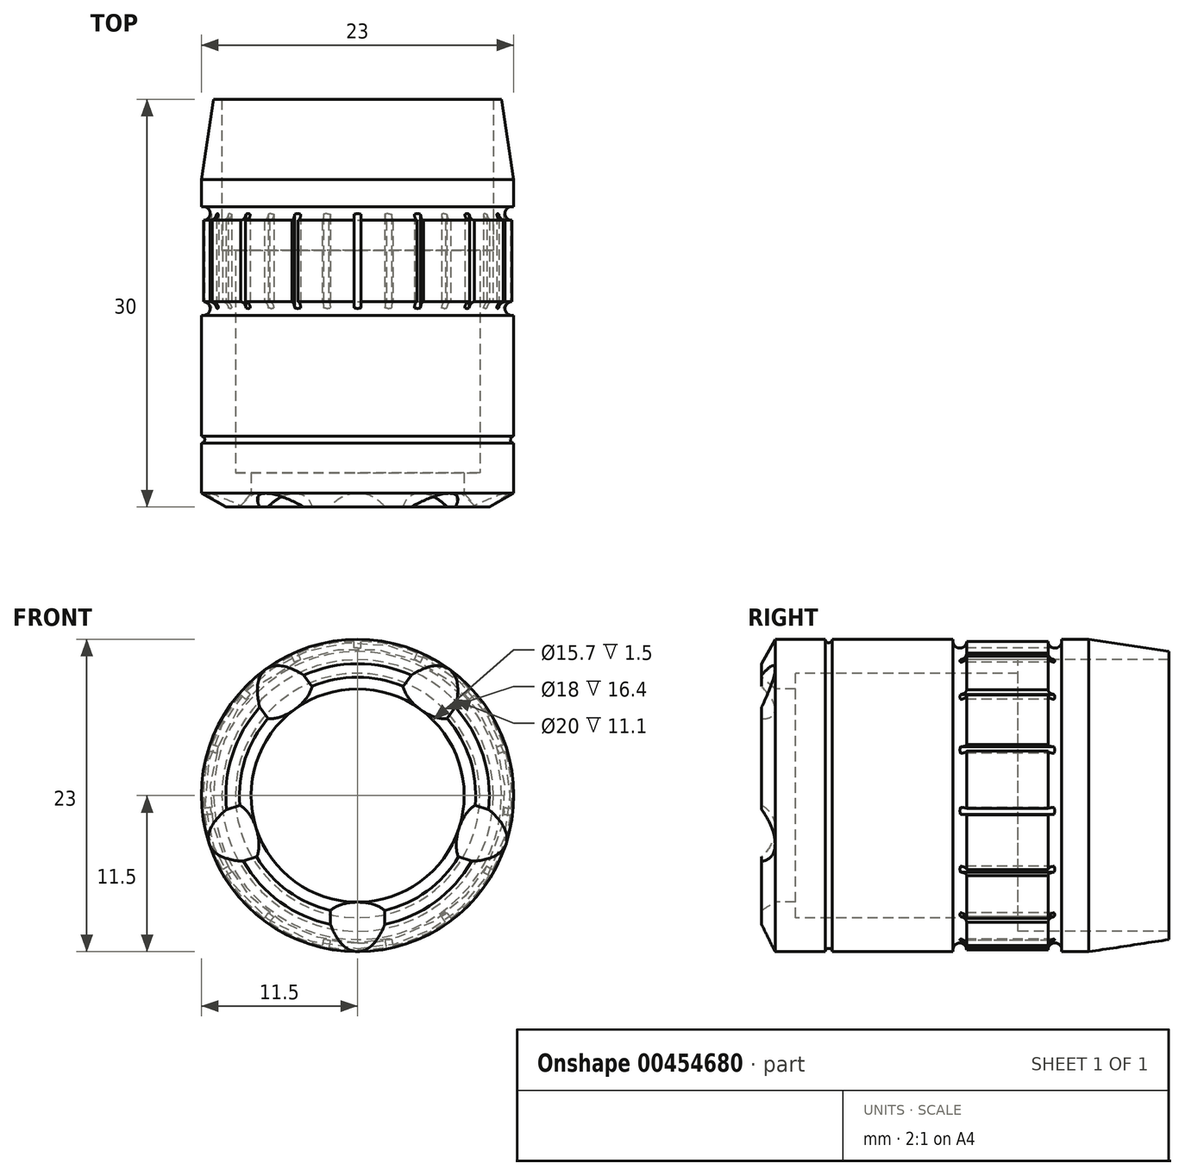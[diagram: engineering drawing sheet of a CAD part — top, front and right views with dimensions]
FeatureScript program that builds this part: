
annotation { "Feature Type Name" : "Feature", "Feature Type Description" : "" }
export const myFeature = defineFeature(function(context is Context, id is Id, definition is map)
    precondition{}
    {
        {
            var Q0;
            Q0=qCreatedBy(makeId("Right.planeOp"),FACE);
            var sketch = newSketch(context, id + "F0", { "sketchPlane" : qUnion([Q0])});
            skLineSegment(sketch, "E0", {"start": v(0, 7.85) * mm, "end": v(0, 11.5) * mm, "construction": true});
            skLineSegment(sketch, "E1", {"start": v(2.5, 7.85) * mm, "end": v(2.5, 9) * mm});
            skLineSegment(sketch, "E2", {"start": v(2.5, 9) * mm, "end": v(18.9, 9) * mm});
            skLineSegment(sketch, "E3", {"start": v(18.9, 9) * mm, "end": v(18.9, 10) * mm});
            skLineSegment(sketch, "E4", {"start": v(18.9, 10) * mm, "end": v(30, 10) * mm});
            skLineSegment(sketch, "E5", {"start": v(30, 10) * mm, "end": v(30, 10.6) * mm});
            skLineSegment(sketch, "E6", {"start": v(30, 10.6) * mm, "end": v(24.1, 11.5) * mm});
            skArc(sketch, "E7", {"start": v(4.7, 11.5) * mm, "mid": v(4.95, 11.25) * mm, "end": v(5.2, 11.5) * mm});
            skLineSegment(sketch, "E8", {"start": v(5.2, 11.5) * mm, "end": v(14.1, 11.5) * mm});
            skLineSegment(sketch, "E9", {"start": v(15.1, 11.35) * mm, "end": v(21.1, 11.35) * mm});
            skArc(sketch, "E10", {"start": v(14.1, 11.35) * mm, "mid": v(14.6, 10.85) * mm, "end": v(15.1, 11.35) * mm});
            skLineSegment(sketch, "E11", {"start": v(14.1, 11.35) * mm, "end": v(14.1, 11.5) * mm});
            skArc(sketch, "E12", {"start": v(21.1, 11.35) * mm, "mid": v(21.6, 10.85) * mm, "end": v(22.1, 11.35) * mm});
            skLineSegment(sketch, "E13", {"start": v(22.1, 11.35) * mm, "end": v(22.1, 11.5) * mm});
            skLineSegment(sketch, "E14", {"start": v(22.1, 11.5) * mm, "end": v(24.1, 11.5) * mm});
            skLineSegment(sketch, "E15", {"start": v(1, 7.85) * mm, "end": v(0, 8.7) * mm});
            skLineSegment(sketch, "E16", {"start": v(1, 11.5) * mm, "end": v(0, 9.7) * mm});
            skLineSegment(sketch, "E17", {"start": v(1, 11.5) * mm, "end": v(4.7, 11.5) * mm});
            skLineSegment(sketch, "E18", {"start": v(1, 7.85) * mm, "end": v(2.5, 7.85) * mm});
            skLineSegment(sketch, "E19", {"start": v(0, 9.7) * mm, "end": v(0, 8.7) * mm});
            skSolve(sketch);
        }
        {
            var Q0;
            Q0=qCreatedBy(makeId("Right.planeOp"),FACE);
            var sketch = newSketch(context, id + "F1", { "sketchPlane" : qUnion([Q0])});
            skLineSegment(sketch, "E20", {"start": v(-7.01, 0) * mm, "end": v(36.18, 0) * mm, "construction": true});
            skSolve(sketch);
        }
        {
            var Q0;
            Q0 = qSketchRegion(id + "F0", true);
            var Q1;
            Q1=sQuery(id+"F1.wireOp",EDGE,"E20");
            revolve(context, id + "F2", {"entities" : qUnion([Q0]), "axis" : qUnion([Q1]), "revolveType" : RevolveType.FULL});
        }
        {
            var Q0;
            Q0=qCreatedBy(makeId("Front.planeOp"),FACE);
            cPlane(context, id + "F3", {"entities" : qUnion([Q0]), "cplaneType" : CPlaneType.OFFSET, "offset" : 14.6 * mm, "oppositeDirection" : true, "width" : 150 * mm, "height" : 150 * mm});
        }
        {
            var Q0;
            Q0=qCreatedBy(id+"F3.planeOp",FACE);
            var sketch = newSketch(context, id + "F4", { "sketchPlane" : qUnion([Q0])});
            skLineSegment(sketch, "E21.bottom", {"start": v(-0.25, 11.6) * mm, "end": v(0.25, 11.6) * mm});
            skLineSegment(sketch, "E21.top", {"start": v(-0.25, 10.85) * mm, "end": v(0.25, 10.85) * mm});
            skLineSegment(sketch, "E21.left", {"start": v(-0.25, 11.6) * mm, "end": v(-0.25, 10.85) * mm});
            skLineSegment(sketch, "E21.right", {"start": v(0.25, 11.6) * mm, "end": v(0.25, 10.85) * mm});
            skLineSegment(sketch, "E22.1.0", {"start": v(-4.5, 10.7) * mm, "end": v(-4.18, 10.01) * mm});
            skLineSegment(sketch, "E22.1.1", {"start": v(-4.95, 10.5) * mm, "end": v(-4.5, 10.7) * mm});
            skLineSegment(sketch, "E22.1.2", {"start": v(-4.95, 10.5) * mm, "end": v(-4.64, 9.81) * mm});
            skLineSegment(sketch, "E22.1.3", {"start": v(-4.64, 9.81) * mm, "end": v(-4.18, 10.01) * mm});
            skLineSegment(sketch, "E22.2.0", {"start": v(-8.45, 7.95) * mm, "end": v(-7.9, 7.45) * mm});
            skLineSegment(sketch, "E22.2.1", {"start": v(-8.79, 7.58) * mm, "end": v(-8.45, 7.95) * mm});
            skLineSegment(sketch, "E22.2.2", {"start": v(-8.79, 7.58) * mm, "end": v(-8.23, 7.07) * mm});
            skLineSegment(sketch, "E22.2.3", {"start": v(-8.23, 7.07) * mm, "end": v(-7.9, 7.45) * mm});
            skLineSegment(sketch, "E22.3.0", {"start": v(-10.96, 3.82) * mm, "end": v(-10.24, 3.6) * mm});
            skLineSegment(sketch, "E22.3.1", {"start": v(-11.11, 3.35) * mm, "end": v(-10.96, 3.82) * mm});
            skLineSegment(sketch, "E22.3.2", {"start": v(-11.11, 3.35) * mm, "end": v(-10.4, 3.12) * mm});
            skLineSegment(sketch, "E22.3.3", {"start": v(-10.4, 3.12) * mm, "end": v(-10.24, 3.6) * mm});
            skLineSegment(sketch, "E22.4.0", {"start": v(-11.56, -0.96) * mm, "end": v(-10.82, -0.89) * mm});
            skLineSegment(sketch, "E22.4.1", {"start": v(-11.51, -1.46) * mm, "end": v(-11.56, -0.96) * mm});
            skLineSegment(sketch, "E22.4.2", {"start": v(-11.51, -1.46) * mm, "end": v(-10.76, -1.38) * mm});
            skLineSegment(sketch, "E22.4.3", {"start": v(-10.76, -1.38) * mm, "end": v(-10.82, -0.89) * mm});
            skLineSegment(sketch, "E22.5.0", {"start": v(-10.17, -5.58) * mm, "end": v(-9.52, -5.2) * mm});
            skLineSegment(sketch, "E22.5.1", {"start": v(-9.92, -6.02) * mm, "end": v(-10.17, -5.58) * mm});
            skLineSegment(sketch, "E22.5.2", {"start": v(-9.92, -6.02) * mm, "end": v(-9.27, -5.64) * mm});
            skLineSegment(sketch, "E22.5.3", {"start": v(-9.27, -5.64) * mm, "end": v(-9.52, -5.2) * mm});
            skLineSegment(sketch, "E22.6.0", {"start": v(-7.02, -9.24) * mm, "end": v(-6.58, -8.63) * mm});
            skLineSegment(sketch, "E22.6.1", {"start": v(-6.62, -9.53) * mm, "end": v(-7.02, -9.24) * mm});
            skLineSegment(sketch, "E22.6.2", {"start": v(-6.62, -9.53) * mm, "end": v(-6.18, -8.92) * mm});
            skLineSegment(sketch, "E22.6.3", {"start": v(-6.18, -8.92) * mm, "end": v(-6.58, -8.63) * mm});
            skLineSegment(sketch, "E22.7.0", {"start": v(-2.66, -11.3) * mm, "end": v(-2.5, -10.56) * mm});
            skLineSegment(sketch, "E22.7.1", {"start": v(-2.17, -11.4) * mm, "end": v(-2.66, -11.3) * mm});
            skLineSegment(sketch, "E22.7.2", {"start": v(-2.17, -11.4) * mm, "end": v(-2.01, -10.66) * mm});
            skLineSegment(sketch, "E22.7.3", {"start": v(-2.01, -10.66) * mm, "end": v(-2.5, -10.56) * mm});
            skLineSegment(sketch, "E22.8.0", {"start": v(2.17, -11.4) * mm, "end": v(2.01, -10.66) * mm});
            skLineSegment(sketch, "E22.8.1", {"start": v(2.66, -11.3) * mm, "end": v(2.17, -11.4) * mm});
            skLineSegment(sketch, "E22.8.2", {"start": v(2.66, -11.3) * mm, "end": v(2.5, -10.56) * mm});
            skLineSegment(sketch, "E22.8.3", {"start": v(2.5, -10.56) * mm, "end": v(2.01, -10.66) * mm});
            skLineSegment(sketch, "E22.9.0", {"start": v(6.62, -9.53) * mm, "end": v(6.18, -8.92) * mm});
            skLineSegment(sketch, "E22.9.1", {"start": v(7.02, -9.24) * mm, "end": v(6.62, -9.53) * mm});
            skLineSegment(sketch, "E22.9.2", {"start": v(7.02, -9.24) * mm, "end": v(6.58, -8.63) * mm});
            skLineSegment(sketch, "E22.9.3", {"start": v(6.58, -8.63) * mm, "end": v(6.18, -8.92) * mm});
            skLineSegment(sketch, "E22.10.0", {"start": v(9.92, -6.02) * mm, "end": v(9.27, -5.64) * mm});
            skLineSegment(sketch, "E22.10.1", {"start": v(10.17, -5.58) * mm, "end": v(9.92, -6.02) * mm});
            skLineSegment(sketch, "E22.10.2", {"start": v(10.17, -5.58) * mm, "end": v(9.52, -5.2) * mm});
            skLineSegment(sketch, "E22.10.3", {"start": v(9.52, -5.2) * mm, "end": v(9.27, -5.64) * mm});
            skLineSegment(sketch, "E22.11.0", {"start": v(11.51, -1.46) * mm, "end": v(10.76, -1.38) * mm});
            skLineSegment(sketch, "E22.11.1", {"start": v(11.56, -0.96) * mm, "end": v(11.51, -1.46) * mm});
            skLineSegment(sketch, "E22.11.2", {"start": v(11.56, -0.96) * mm, "end": v(10.82, -0.89) * mm});
            skLineSegment(sketch, "E22.11.3", {"start": v(10.82, -0.89) * mm, "end": v(10.76, -1.38) * mm});
            skLineSegment(sketch, "E22.12.0", {"start": v(11.11, 3.35) * mm, "end": v(10.4, 3.12) * mm});
            skLineSegment(sketch, "E22.12.1", {"start": v(10.96, 3.82) * mm, "end": v(11.11, 3.35) * mm});
            skLineSegment(sketch, "E22.12.2", {"start": v(10.96, 3.82) * mm, "end": v(10.24, 3.6) * mm});
            skLineSegment(sketch, "E22.12.3", {"start": v(10.24, 3.6) * mm, "end": v(10.4, 3.12) * mm});
            skLineSegment(sketch, "E22.13.0", {"start": v(8.79, 7.58) * mm, "end": v(8.23, 7.07) * mm});
            skLineSegment(sketch, "E22.13.1", {"start": v(8.45, 7.95) * mm, "end": v(8.79, 7.58) * mm});
            skLineSegment(sketch, "E22.13.2", {"start": v(8.45, 7.95) * mm, "end": v(7.9, 7.45) * mm});
            skLineSegment(sketch, "E22.13.3", {"start": v(7.9, 7.45) * mm, "end": v(8.23, 7.07) * mm});
            skLineSegment(sketch, "E22.14.0", {"start": v(4.95, 10.5) * mm, "end": v(4.64, 9.81) * mm});
            skLineSegment(sketch, "E22.14.1", {"start": v(4.5, 10.7) * mm, "end": v(4.95, 10.5) * mm});
            skLineSegment(sketch, "E22.14.2", {"start": v(4.5, 10.7) * mm, "end": v(4.18, 10.01) * mm});
            skLineSegment(sketch, "E22.14.3", {"start": v(4.18, 10.01) * mm, "end": v(4.64, 9.81) * mm});
            skPoint(sketch, "E22.center", {"position": v(0, 0) * mm});
            skSolve(sketch);
        }
        {
            var Q0;
            Q0 = qSketchRegion(id + "F4", true);
            extrude(context, id + "F5", {"entities" : qUnion([Q0]), "operationType" : NewBodyOperationType.REMOVE, "oppositeDirection" : true, "depth" : 7 * mm});
        }
        {
            var Q0;
            Q0=qCreatedBy(makeId("Top.planeOp"),FACE);
            var sketch = newSketch(context, id + "F6", { "sketchPlane" : qUnion([Q0])});
            skArc(sketch, "E23", {"start": v(2, 0) * mm, "mid": v(0, 1) * mm, "end": v(-2, 0) * mm});
            skLineSegment(sketch, "E24", {"start": v(-2, 0) * mm, "end": v(2, 0) * mm});
            skSolve(sketch);
        }
        {
            var Q0;
            Q0 = qSketchRegion(id + "F6", true);
            extrude(context, id + "F7", {"entities" : qUnion([Q0]), "operationType" : NewBodyOperationType.REMOVE, "oppositeDirection" : true, "depth" : 25 * mm});
        }
        {
            var Q0;
            Q0=qCreatedBy(makeId("Top.planeOp"),FACE);
            var Q1;
            Q1=sQuery(id+"F1.wireOp",EDGE,"E20");
            cPlane(context, id + "F8", {"entities" : qUnion([Q0, Q1]), "cplaneType" : CPlaneType.LINE_ANGLE, "offset" : 25 * mm, "angle" : 72 * degree, "width" : 150 * mm, "height" : 150 * mm});
        }
        {
            var Q0;
            Q0=qCreatedBy(id+"F8.planeOp",FACE);
            var sketch = newSketch(context, id + "F9", { "sketchPlane" : qUnion([Q0])});
            skArc(sketch, "E25", {"start": v(0, 2) * mm, "mid": v(-1, 0) * mm, "end": v(0, -2) * mm});
            skLineSegment(sketch, "E26", {"start": v(0, 2) * mm, "end": v(0, -2) * mm});
            skSolve(sketch);
        }
        {
            var Q0;
            Q0 = qSketchRegion(id + "F9", true);
            extrude(context, id + "F10", {"entities" : qUnion([Q0]), "operationType" : NewBodyOperationType.REMOVE, "depth" : 25 * mm});
        }
        {
            var Q0;
            Q0=qCreatedBy(id+"F8.planeOp",FACE);
            var Q1;
            Q1=sQuery(id+"F1.wireOp",EDGE,"E20");
            cPlane(context, id + "F11", {"entities" : qUnion([Q0, Q1]), "cplaneType" : CPlaneType.LINE_ANGLE, "offset" : 25 * mm, "angle" : 72 * degree, "width" : 150 * mm, "height" : 150 * mm});
        }
        {
            var Q0;
            Q0=qCreatedBy(id+"F11.planeOp",FACE);
            var sketch = newSketch(context, id + "F12", { "sketchPlane" : qUnion([Q0])});
            skArc(sketch, "E27", {"start": v(-2, 0) * mm, "mid": v(0, -1) * mm, "end": v(2, 0) * mm});
            skLineSegment(sketch, "E28", {"start": v(-2, 0) * mm, "end": v(2, 0) * mm});
            skSolve(sketch);
        }
        {
            var Q0;
            Q0 = qSketchRegion(id + "F12", true);
            extrude(context, id + "F13", {"entities" : qUnion([Q0]), "operationType" : NewBodyOperationType.REMOVE, "oppositeDirection" : true, "depth" : 25 * mm});
        }
        {
            var Q0;
            Q0=qCreatedBy(id+"F11.planeOp",FACE);
            var Q1;
            Q1=sQuery(id+"F1.wireOp",EDGE,"E20");
            cPlane(context, id + "F14", {"entities" : qUnion([Q0, Q1]), "cplaneType" : CPlaneType.LINE_ANGLE, "offset" : 25 * mm, "angle" : 72 * degree, "width" : 150 * mm, "height" : 150 * mm});
        }
        {
            var Q0;
            Q0=qCreatedBy(id+"F14.planeOp",FACE);
            var sketch = newSketch(context, id + "F15", { "sketchPlane" : qUnion([Q0])});
            skArc(sketch, "E29", {"start": v(2, 0) * mm, "mid": v(0, 1) * mm, "end": v(-2, 0) * mm});
            skLineSegment(sketch, "E30", {"start": v(-2, 0) * mm, "end": v(2, 0) * mm});
            skSolve(sketch);
        }
        {
            var Q0;
            Q0 = qSketchRegion(id + "F15", true);
            extrude(context, id + "F16", {"entities" : qUnion([Q0]), "operationType" : NewBodyOperationType.REMOVE, "depth" : 25 * mm});
        }
        {
            var Q0;
            Q0=qCreatedBy(id+"F14.planeOp",FACE);
            var Q1;
            Q1=sQuery(id+"F1.wireOp",EDGE,"E20");
            cPlane(context, id + "F17", {"entities" : qUnion([Q0, Q1]), "cplaneType" : CPlaneType.LINE_ANGLE, "offset" : 25 * mm, "angle" : 72 * degree, "width" : 150 * mm, "height" : 150 * mm});
        }
        {
            var Q0;
            Q0=qCreatedBy(id+"F17.planeOp",FACE);
            var sketch = newSketch(context, id + "F18", { "sketchPlane" : qUnion([Q0])});
            skArc(sketch, "E31", {"start": v(0, 2) * mm, "mid": v(-1, 0) * mm, "end": v(0, -2) * mm});
            skLineSegment(sketch, "E32", {"start": v(0, -2) * mm, "end": v(0, 2) * mm});
            skSolve(sketch);
        }
        {
            var Q0;
            Q0 = qSketchRegion(id + "F18", true);
            extrude(context, id + "F19", {"entities" : qUnion([Q0]), "operationType" : NewBodyOperationType.REMOVE, "oppositeDirection" : true, "depth" : 25 * mm});
        }
    });
